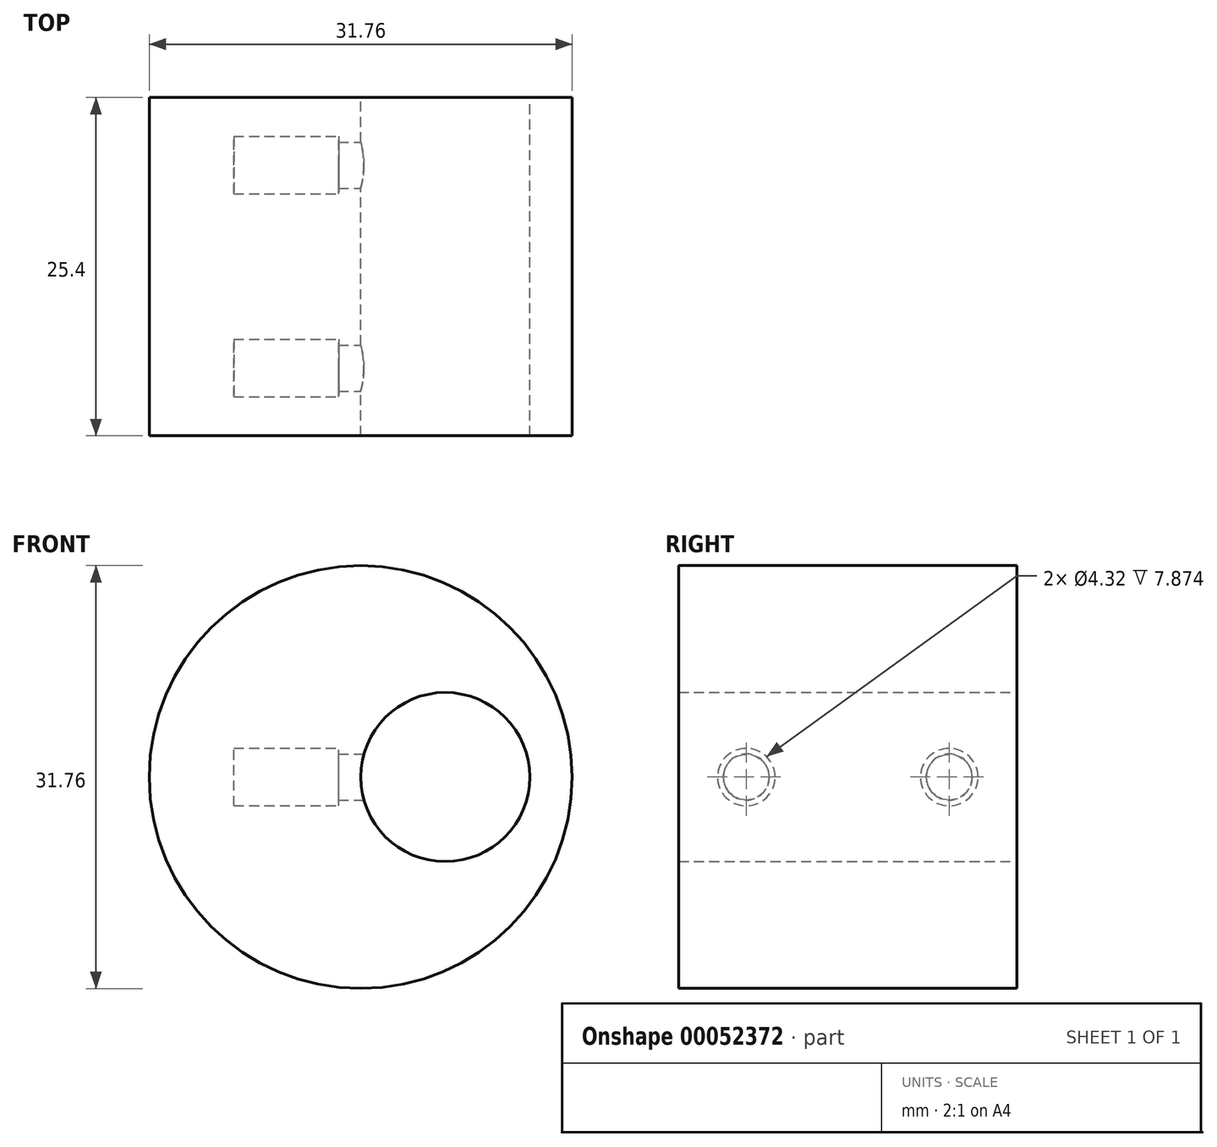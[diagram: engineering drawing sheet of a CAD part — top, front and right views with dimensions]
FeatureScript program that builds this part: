
annotation { "Feature Type Name" : "Feature", "Feature Type Description" : "" }
export const myFeature = defineFeature(function(context is Context, id is Id, definition is map)
    precondition{}
    {
        {
            var Q0;
            Q0=qCreatedBy(makeId("Front.planeOp"),FACE);
            var sketch = newSketch(context, id + "F0", { "sketchPlane" : qUnion([Q0])});
            skCircle(sketch, "E0", {"center": v(-6.35, 0) * mm, "radius": 15.88 * mm});
            skCircle(sketch, "E1", {"center": v(0, 0) * mm, "radius": 6.35 * mm});
            skSolve(sketch);
        }
        {
            var Q0;
            Q0 = qSketchRegion(id + "F0", true);
            extrude(context, id + "F1", {"entities" : qUnion([Q0]), "depth" : 25.4 * mm, "symmetric" : true});
        }
        {
            var Q0;
            Q0=qCreatedBy(makeId("Right.planeOp"),FACE);
            cPlane(context, id + "F2", {"entities" : qUnion([Q0]), "cplaneType" : CPlaneType.OFFSET, "offset" : 15.88 * mm, "oppositeDirection" : true, "width" : 152.4 * mm, "height" : 152.4 * mm});
        }
        {
            var Q0;
            Q0=qCreatedBy(id+"F2.planeOp",FACE);
            var sketch = newSketch(context, id + "F3", { "sketchPlane" : qUnion([Q0])});
            skPoint(sketch, "E2", {"position": v(7.62, 0) * mm});
            skPoint(sketch, "E3", {"position": v(-7.62, 0) * mm});
            skSolve(sketch);
        }
        {
            var Q0;
            Q0=sQuery(id+"F3.wireOp",VERTEX,"E2");
            var Q1;
            Q1=sQuery(id+"F3.wireOp",VERTEX,"E3");
            var Q2;
            Q2=makeQuery(id+"F1.opExtrude","SWEPT_BODY",BODY,{"disambiguationData":[OSD([sQuery(id+"F0.wireOp",EDGE,"E0"),sQuery(id+"F0.wireOp",EDGE,"E1")])]});
            hole(context, id + "F4", {"style" : HoleStyle.C_BORE, "holeDiameter" : 3.45 * mm, "cBoreDiameter" : 4.32 * mm, "cBoreDepth" : 7.87 * mm, "endStyle" : HoleEndStyle.BLIND, "oppositeDirection" : true, "holeDepth" : 19.05 * mm, "locations" : qUnion([Q0, Q1]), "scope" : qUnion([Q2])});
        }
    });
